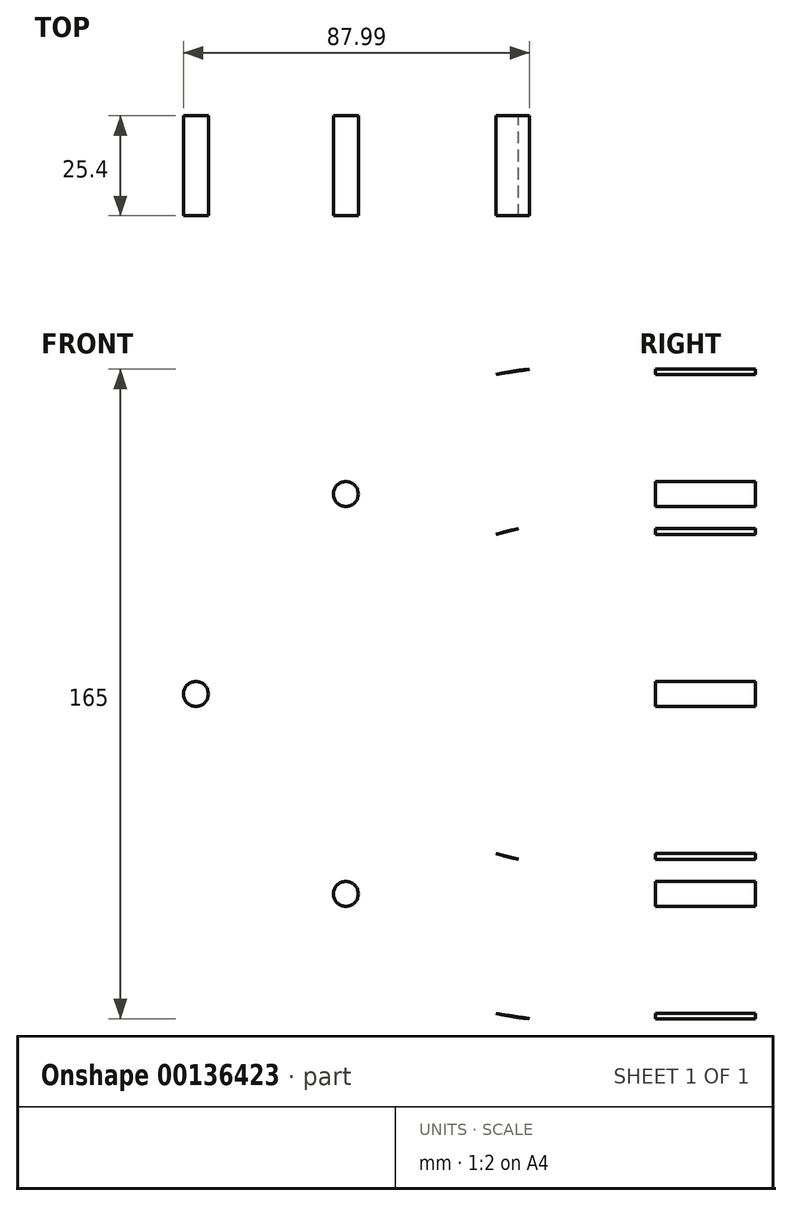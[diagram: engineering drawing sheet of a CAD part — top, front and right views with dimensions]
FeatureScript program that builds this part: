
annotation { "Feature Type Name" : "Feature", "Feature Type Description" : "" }
export const myFeature = defineFeature(function(context is Context, id is Id, definition is map)
    precondition{}
    {
        {
            var Q0;
            Q0=qCreatedBy(makeId("Front.planeOp"),FACE);
            var sketch = newSketch(context, id + "F0", { "sketchPlane" : qUnion([Q0])});
            skLineSegment(sketch, "E0.bottom", {"start": v(228.6, -101.6) * mm, "end": v(-228.6, -101.6) * mm, "construction": true});
            skLineSegment(sketch, "E0.left", {"start": v(228.6, -101.6) * mm, "end": v(228.6, 101.6) * mm, "construction": true});
            skLineSegment(sketch, "E0.right", {"start": v(-228.6, -101.6) * mm, "end": v(-228.6, 101.6) * mm, "construction": true});
            skPoint(sketch, "E0.middle", {"position": v(0, 0) * mm});
            skLineSegment(sketch, "E1", {"start": v(-228.6, 0) * mm, "end": v(228.6, 0) * mm, "construction": true});
            skEllipse(sketch, "E2", {"center": v(0, 0) * mm, "majorRadius": 228.6 * mm, "minorRadius": 101.6 * mm, "majorAxis": v(1, 0), "construction": true});
            skLineSegment(sketch, "E3.0", {"start": v(-228.6, 50.8) * mm, "end": v(228.86, 50.8) * mm, "construction": true});
            skFitSpline(sketch, "E4", {"points": [v(-228.6, 0) * mm, v(0.12, 50.8) * mm], "startDerivative": vector(-0.02, 152.4) * mm, "endDerivative": vector(467.3, 0) * mm});
            skFitSpline(sketch, "E5.MirrorCS", {"points": [v(-228.6, 0) * mm, v(0.12, -50.8) * mm], "startDerivative": vector(-0.02, -152.4) * mm, "endDerivative": vector(467.3, 0) * mm});
            skLineSegment(sketch, "E6.0", {"start": v(-304.8, -101.6) * mm, "end": v(-304.8, 101.6) * mm, "construction": true});
            skFitSpline(sketch, "E7", {"points": [v(-304.8, 0) * mm, v(0, 88.9) * mm], "startDerivative": vector(0, 304.8) * mm, "endDerivative": vector(240.47, 1.05) * mm});
            skFitSpline(sketch, "E8.MirrorCS", {"points": [v(-304.8, 0) * mm, v(0, -88.9) * mm], "startDerivative": vector(0, -304.8) * mm, "endDerivative": vector(240.47, -1.05) * mm});
            skLineSegment(sketch, "E9.0", {"start": v(-189.65, 101.56) * mm, "end": v(-198.16, -101.28) * mm, "construction": true});
            skLineSegment(sketch, "E10.0", {"start": v(-266.7, -101.6) * mm, "end": v(-266.7, 101.6) * mm, "construction": true});
            skCircle(sketch, "E11", {"center": v(-228.6, 50.8) * mm, "radius": 3.18 * mm});
            skCircle(sketch, "E12", {"center": v(-266.7, 0) * mm, "radius": 3.17 * mm});
            skCircle(sketch, "E13.MirrorC", {"center": v(-228.6, -50.8) * mm, "radius": 3.18 * mm});
            skLineSegment(sketch, "E14", {"start": v(0, 101.6) * mm, "end": v(0, -101.6) * mm, "construction": true});
            skFitSpline(sketch, "E15", {"points": [v(-190.5, 81.2) * mm, v(-171.03, 79.56) * mm, v(-166.3, 53.65) * mm, v(-190.5, 40.55) * mm], "startDerivative": vector(72.95, 14.02) * mm, "endDerivative": vector(-86.73, -21.71) * mm});
            skFitSpline(sketch, "E16.MirrorCS", {"points": [v(-190.5, -81.2) * mm, v(-171.03, -79.56) * mm, v(-166.3, -53.65) * mm, v(-190.5, -40.55) * mm], "startDerivative": vector(72.95, -14.02) * mm, "endDerivative": vector(-86.73, 21.71) * mm});
            skSolve(sketch);
        }
        {
            var Q0;
            Q0=qSketchRegion(id+"F0",true);
            extrude(context, id + "F1", {"entities" : qUnion([Q0]), "depth" : 25.4 * mm});
        }
    });
